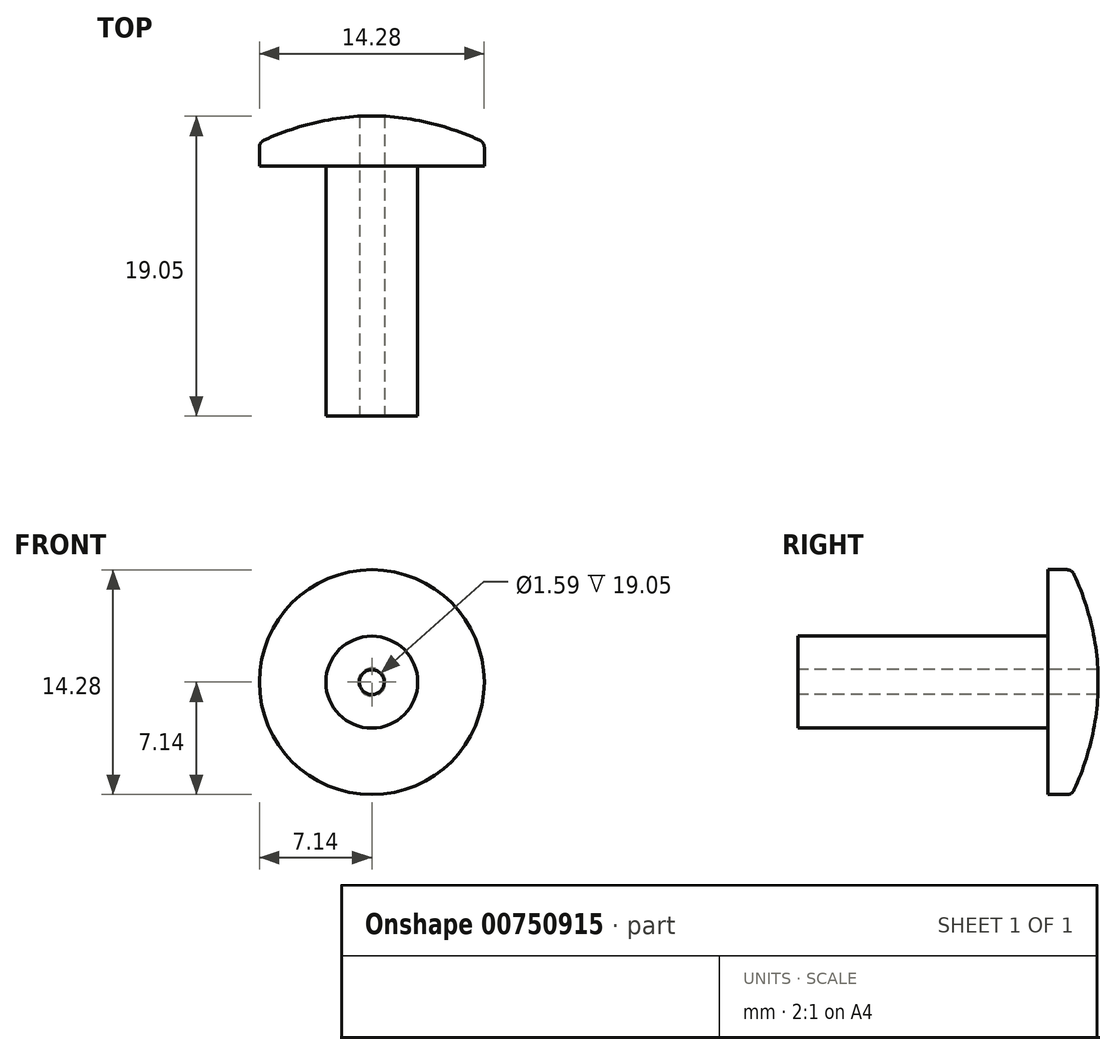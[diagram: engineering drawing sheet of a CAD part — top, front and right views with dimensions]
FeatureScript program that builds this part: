
annotation { "Feature Type Name" : "Feature", "Feature Type Description" : "" }
export const myFeature = defineFeature(function(context is Context, id is Id, definition is map)
    precondition{}
    {
        {
            var Q0;
            Q0=qCreatedBy(makeId("Front.planeOp"),FACE);
            var sketch = newSketch(context, id + "F0", { "sketchPlane" : qUnion([Q0])});
            skCircle(sketch, "E0", {"center": v(0, 0) * mm, "radius": 2.92 * mm});
            skSolve(sketch);
        }
        {
            var Q0;
            Q0 = qSketchRegion(id + "F0", true);
            extrude(context, id + "F1", {"entities" : qUnion([Q0]), "oppositeDirection" : true, "depth" : 19.05 * mm, "offsetDistance" : 25.4 * mm});
        }
        {
            var Q0;
            Q0=makeQuery(id+"F1.opExtrude","CAP_FACE",FACE,{"disambiguationData":[OSD([sQuery(id+"F0.wireOp",EDGE,"E0")])],"isStart":false});
            var sketch = newSketch(context, id + "F2", { "sketchPlane" : qUnion([Q0])});
            skCircle(sketch, "E1", {"center": v(0, 0) * mm, "radius": 7.14 * mm});
            skSolve(sketch);
        }
        {
            var Q0;
            Q0=makeQuery(id+"F2.imprint","IMPRINT",FACE,{"disambiguationData":[TD([[makeQuery(id+"F2.imprint","IMPRINT",EDGE,{"derivedFrom":sQuery(id+"F2.wireOp",EDGE,"E1")}),1.0]])]});
            var Q1;
            Q1=makeQuery(id+"F2.imprint","IMPRINT",FACE,{"disambiguationData":[TD([[makeQuery(id+"F2.imprint","IMPRINT",EDGE,{"derivedFrom":sQuery(id+"F2.wireOp",EDGE,"hCcHzBDb-aXpz-Sch1-wDbs-gP90HNGPvPxa")}),-1.0]])]});
            extrude(context, id + "F3", {"entities" : qUnion([Q0, Q1]), "operationType" : NewBodyOperationType.ADD, "oppositeDirection" : true, "depth" : 3.17 * mm, "offsetDistance" : 25.4 * mm});
        }
        {
            var Q0;
            Q0=makeQuery(id+"F1.opExtrude","CAP_FACE",FACE,{"disambiguationData":[OSD([sQuery(id+"F0.wireOp",EDGE,"E0")])],"isStart":true});
            var sketch = newSketch(context, id + "F4", { "sketchPlane" : qUnion([Q0])});
            skCircle(sketch, "E2", {"center": v(0, 0) * mm, "radius": 0.8 * mm});
            skSolve(sketch);
        }
        {
            var Q0;
            Q0 = qSketchRegion(id + "F4", true);
            extrude(context, id + "F5", {"entities" : qUnion([Q0]), "operationType" : NewBodyOperationType.REMOVE, "endBound" : BoundingType.THROUGH_ALL, "oppositeDirection" : true, "depth" : 25.4 * mm, "offsetDistance" : 25.4 * mm});
        }
        {
            var Q0;
            Q0=qCreatedBy(makeId("Right.planeOp"),FACE);
            var sketch = newSketch(context, id + "F6", { "sketchPlane" : qUnion([Q0])});
            skArc(sketch, "E3", {"start": v(17.34, -7.27) * mm, "mid": v(18.61, -3.73) * mm, "end": v(19.09, 0) * mm});
            skLineSegment(sketch, "E4", {"start": v(17.34, -7.27) * mm, "end": v(21.63, -7.27) * mm});
            skLineSegment(sketch, "E5", {"start": v(0, 0) * mm, "end": v(25.98, 0) * mm, "construction": true});
            skLineSegment(sketch, "E6.0", {"start": v(21.63, 0) * mm, "end": v(21.63, -7.27) * mm});
            skLineSegment(sketch, "E7", {"start": v(19.09, 0) * mm, "end": v(21.63, 0) * mm});
            skSolve(sketch);
        }
        {
            var Q0;
            Q0 = qSketchRegion(id + "F6", true);
            var Q1;
            Q1=sQuery(id+"F6.wireOp",EDGE,"E5");
            revolve(context, id + "F7", {"operationType" : NewBodyOperationType.REMOVE, "surfaceOperationType" : NewSurfaceOperationType.NEW, "entities" : qUnion([Q0]), "axis" : qUnion([Q1]), "revolveType" : RevolveType.FULL, "oppositeDirection" : true});
        }
        {
            var Q0;
            Q0=makeQuery(id+"F7.boolean.opBoolean","INTERSECT",EDGE,{"derivedFrom":[makeQuery(id+"F3.opExtrude","SWEPT_FACE",FACE,{"disambiguationData":[OSD([sQuery(id+"F2.wireOp",EDGE,"E1")])]}),makeQuery(id+"F7.opRevolve","SWEPT_FACE",FACE,{"disambiguationData":[OSD([sQuery(id+"F6.wireOp",EDGE,"E3")])]})]});
            fillet(context, id + "F8", {"entities" : qUnion([Q0]), "radius" : 0.5 * mm, "tangentPropagation" : true, "allowEdgeOverflow" : false});
        }
    });
